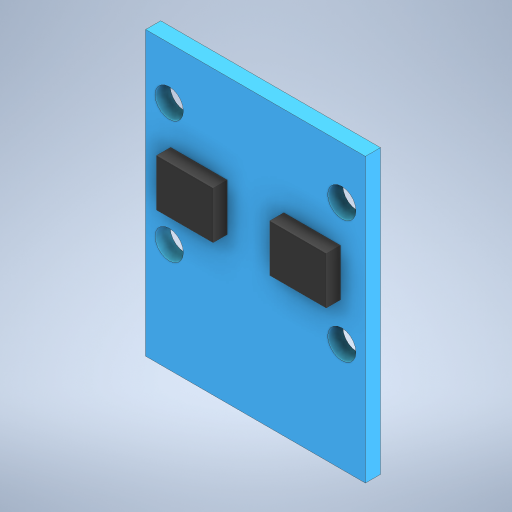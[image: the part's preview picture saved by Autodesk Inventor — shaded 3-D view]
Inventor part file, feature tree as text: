
AUTODESK INVENTOR PART (.ipt)
format: ipt  version: 2023.1 (Build 271208000, 208)  size: 276,480 bytes
history: native  units: mm
features: extrude x2, sketch x2, other x1
ambient origin geometry x8: Origin, YZ Plane, XZ Plane, XY Plane, X Axis, Y Axis, Z Axis, Center Point
bodies: Body1 (feature_tree)
feature tree (5):
  other  "솔리드1"
  extrude  "돌출1"  Depth=23.3mm
  extrude  "돌출2"  Depth=30.0mm
  sketch  "스케치1"
  sketch  "스케치2"
